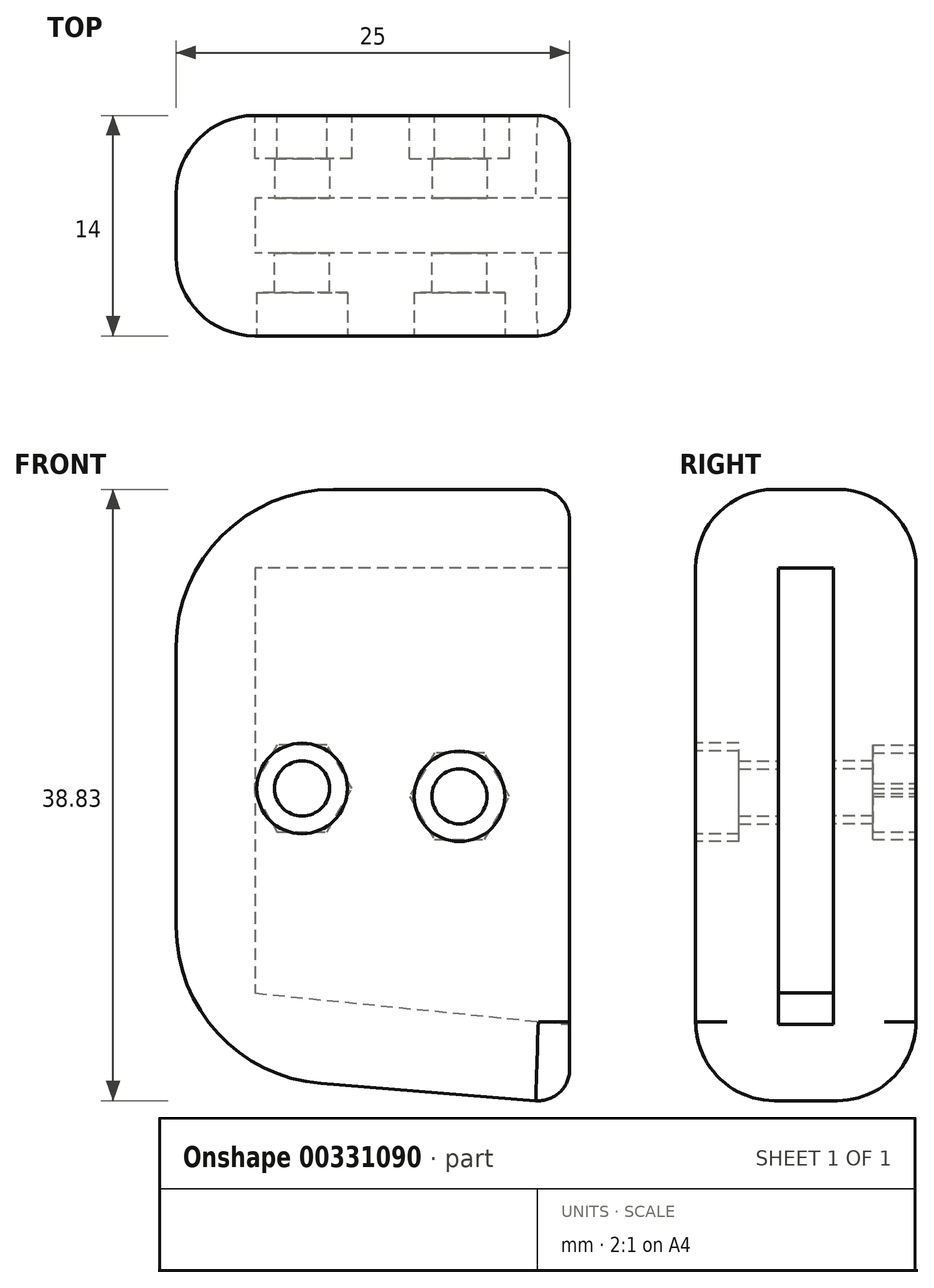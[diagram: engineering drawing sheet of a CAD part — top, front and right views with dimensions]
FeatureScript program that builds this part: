
annotation { "Feature Type Name" : "Feature", "Feature Type Description" : "" }
export const myFeature = defineFeature(function(context is Context, id is Id, definition is map)
    precondition{}
    {
        {
            var Q0;
            Q0=qCreatedBy(makeId("Front.planeOp"),FACE);
            var sketch = newSketch(context, id + "F0", { "sketchPlane" : qUnion([Q0])});
            skLineSegment(sketch, "E0", {"start": v(0, 0) * mm, "end": v(25, 0) * mm});
            skLineSegment(sketch, "E1", {"start": v(25, 0) * mm, "end": v(25, -39) * mm});
            skLineSegment(sketch, "E2", {"start": v(25, -39) * mm, "end": v(0, -37) * mm});
            skLineSegment(sketch, "E3", {"start": v(0, -37) * mm, "end": v(0, 0) * mm});
            skSolve(sketch);
        }
        {
            var Q0;
            Q0=makeQuery(id+"F0.imprint","IMPRINT",FACE,{"disambiguationData":[TD([[makeQuery(id+"F0.imprint","IMPRINT",EDGE,{"derivedFrom":sQuery(id+"F0.wireOp",EDGE,"E0")}),-1.0]])]});
            extrude(context, id + "F1", {"entities" : qUnion([Q0]), "depth" : 7 * mm});
        }
        {
            var Q0;
            Q0=makeQuery(id+"F1.opExtrude","CAP_FACE",FACE,{"disambiguationData":[OSD([sQuery(id+"F0.wireOp",EDGE,"E0"),sQuery(id+"F0.wireOp",EDGE,"E1"),sQuery(id+"F0.wireOp",EDGE,"E2"),sQuery(id+"F0.wireOp",EDGE,"E3")])],"isStart":false});
            var sketch = newSketch(context, id + "F2", { "sketchPlane" : qUnion([Q0])});
            skLineSegment(sketch, "E4", {"start": v(25, -5) * mm, "end": v(5, -5) * mm});
            skLineSegment(sketch, "E5", {"start": v(5, -5) * mm, "end": v(5, -32) * mm});
            skLineSegment(sketch, "E6", {"start": v(5, -32) * mm, "end": v(25, -34) * mm});
            skSolve(sketch);
        }
        {
            var Q0;
            {var subQ0=sQuery(id+"F2.wireOp",EDGE,"E4");Q0=makeQuery(id+"F2.imprint","IMPRINT",FACE,{"disambiguationData":[TD([[makeQuery(id+"F2.imprint","IMPRINT",EDGE,{"derivedFrom":subQ0}),1.0]])]});}
            extrude(context, id + "F3", {"entities" : qUnion([Q0]), "operationType" : NewBodyOperationType.REMOVE, "oppositeDirection" : true, "depth" : 1.75 * mm});
        }
        {
            var Q0;
            Q0=makeQuery(id+"F3.boolean.opBoolean","COPY",FACE,{"derivedFrom":makeQuery(id+"F3.opExtrude","CAP_FACE",FACE,{"disambiguationData":[OSD([sQuery(id+"F0.wireOp",EDGE,"E1"),sQuery(id+"F2.wireOp",EDGE,"E4"),sQuery(id+"F2.wireOp",EDGE,"E5"),sQuery(id+"F2.wireOp",EDGE,"E6")])],"isStart":false})});
            var sketch = newSketch(context, id + "F4", { "sketchPlane" : qUnion([Q0])});
            skLineSegment(sketch, "E7", {"start": v(25, -19.5) * mm, "end": v(5, -19.5) * mm, "construction": true});
            skCircle(sketch, "E8", {"center": v(18, -19.5) * mm, "radius": 1.75 * mm});
            skLineSegment(sketch, "E9", {"start": v(25, -19) * mm, "end": v(5, -19) * mm, "construction": true});
            skCircle(sketch, "E10", {"center": v(8, -19) * mm, "radius": 1.75 * mm});
            skSolve(sketch);
        }
        {
            var Q0;
            Q0=makeQuery(id+"F4.imprint","IMPRINT",FACE,{"disambiguationData":[TD([[makeQuery(id+"F4.imprint","IMPRINT",EDGE,{"derivedFrom":sQuery(id+"F4.wireOp",EDGE,"E10")}),1.0]])]});
            var Q1;
            Q1=makeQuery(id+"F4.imprint","IMPRINT",FACE,{"disambiguationData":[TD([[makeQuery(id+"F4.imprint","IMPRINT",EDGE,{"derivedFrom":sQuery(id+"F4.wireOp",EDGE,"E8")}),1.0]])]});
            extrude(context, id + "F5", {"entities" : qUnion([Q0, Q1]), "operationType" : NewBodyOperationType.REMOVE, "oppositeDirection" : true, "depth" : 5.25 * mm});
        }
        {
            var Q0;
            Q0=makeQuery(id+"F1.opExtrude","SWEPT_BODY",BODY,{"disambiguationData":[OSD([sQuery(id+"F0.wireOp",EDGE,"E0"),sQuery(id+"F0.wireOp",EDGE,"E1"),sQuery(id+"F0.wireOp",EDGE,"E2"),sQuery(id+"F0.wireOp",EDGE,"E3")])]});
            var Q1;
            Q1=makeQuery(id+"F1.opExtrude","CAP_FACE",FACE,{"disambiguationData":[OSD([sQuery(id+"F0.wireOp",EDGE,"E0"),sQuery(id+"F0.wireOp",EDGE,"E1"),sQuery(id+"F0.wireOp",EDGE,"E2"),sQuery(id+"F0.wireOp",EDGE,"E3")])],"isStart":false});
            mirror(context, id + "F6", {"operationType" : NewBodyOperationType.ADD, "entities" : qUnion([Q0]), "mirrorPlane" : qUnion([Q1])});
        }
        {
            var Q0;
            {var subQ0=makeQuery(id+"F1.opExtrude","SWEPT_EDGE",EDGE,{"disambiguationData":[OSD([sQuery(id+"F0.wireOp",EDGE,"E0"),sQuery(id+"F0.wireOp",EDGE,"E3")])]});Q0=makeQuery(id+"F6.boolean.opBoolean","MERGE",EDGE,{"derivedFrom":[subQ0,makeQuery(id+"F6.opPattern","COPY",EDGE,{"derivedFrom":subQ0,"instanceName":"1"})]});}
            var Q1;
            {var subQ0=makeQuery(id+"F1.opExtrude","SWEPT_EDGE",EDGE,{"disambiguationData":[OSD([sQuery(id+"F0.wireOp",EDGE,"E2"),sQuery(id+"F0.wireOp",EDGE,"E3")])]});Q1=makeQuery(id+"F6.boolean.opBoolean","MERGE",EDGE,{"derivedFrom":[subQ0,makeQuery(id+"F6.opPattern","COPY",EDGE,{"derivedFrom":subQ0,"instanceName":"1"})]});}
            fillet(context, id + "F7", {"entities" : qUnion([Q0, Q1]), "radius" : 10 * mm, "tangentPropagation" : true, "allowEdgeOverflow" : false});
        }
        {
            var Q0;
            Q0=makeQuery(id+"F6.opPattern","COPY",EDGE,{"derivedFrom":makeQuery(id+"F1.opExtrude","CAP_EDGE",EDGE,{"disambiguationData":[OSD([sQuery(id+"F0.wireOp",EDGE,"E0")])],"isStart":true}),"instanceName":"1"});
            var Q1;
            Q1=makeQuery(id+"F1.opExtrude","CAP_EDGE",EDGE,{"disambiguationData":[OSD([sQuery(id+"F0.wireOp",EDGE,"E0")])],"isStart":true});
            fillet(context, id + "F8", {"entities" : qUnion([Q0, Q1]), "radius" : 5 * mm, "tangentPropagation" : true, "allowEdgeOverflow" : false});
        }
        {
            var Q0;
            Q0=makeQuery(id+"F6.opPattern","COPY",EDGE,{"derivedFrom":makeQuery(id+"F1.opExtrude","CAP_EDGE",EDGE,{"disambiguationData":[OSD([sQuery(id+"F0.wireOp",EDGE,"E1")])],"isStart":true}),"instanceName":"1"});
            fillet(context, id + "F9", {"entities" : qUnion([Q0]), "radius" : 2 * mm, "tangentPropagation" : true, "allowEdgeOverflow" : false});
        }
        {
            var Q0;
            Q0=makeQuery(id+"F6.opPattern","COPY",FACE,{"derivedFrom":makeQuery(id+"F1.opExtrude","CAP_FACE",FACE,{"disambiguationData":[OSD([sQuery(id+"F0.wireOp",EDGE,"E0"),sQuery(id+"F0.wireOp",EDGE,"E1"),sQuery(id+"F0.wireOp",EDGE,"E2"),sQuery(id+"F0.wireOp",EDGE,"E3")])],"isStart":true}),"instanceName":"1"});
            var sketch = newSketch(context, id + "F10", { "sketchPlane" : qUnion([Q0])});
            skCircle(sketch, "E11", {"center": v(8, -19) * mm, "radius": 2.88 * mm});
            skCircle(sketch, "E12", {"center": v(18, -19.5) * mm, "radius": 2.88 * mm});
            skSolve(sketch);
        }
        {
            var Q0;
            Q0=makeQuery(id+"F10.imprint","IMPRINT",FACE,{"disambiguationData":[TD([[makeQuery(id+"F10.imprint","IMPRINT",EDGE,{"derivedFrom":sQuery(id+"F10.wireOp",EDGE,"E11")}),1.0]])]});
            var Q1;
            Q1=makeQuery(id+"F10.imprint","IMPRINT",FACE,{"disambiguationData":[TD([[makeQuery(id+"F10.imprint","IMPRINT",EDGE,{"derivedFrom":sQuery(id+"F10.wireOp",EDGE,"E12")}),1.0]])]});
            extrude(context, id + "F11", {"entities" : qUnion([Q0, Q1]), "operationType" : NewBodyOperationType.REMOVE, "oppositeDirection" : true, "depth" : 2.75 * mm});
        }
        {
            var Q0;
            Q0=makeQuery(id+"F1.opExtrude","CAP_FACE",FACE,{"disambiguationData":[OSD([sQuery(id+"F0.wireOp",EDGE,"E0"),sQuery(id+"F0.wireOp",EDGE,"E1"),sQuery(id+"F0.wireOp",EDGE,"E2"),sQuery(id+"F0.wireOp",EDGE,"E3")])],"isStart":true});
            var sketch = newSketch(context, id + "F12", { "sketchPlane" : qUnion([Q0])});
            skCircle(sketch, "E13.cCircle", {"center": v(-18, -19.5) * mm, "radius": 2.75 * mm, "construction": true});
            skLineSegment(sketch, "E13.0", {"start": v(-19.59, -16.75) * mm, "end": v(-16.41, -16.75) * mm});
            skLineSegment(sketch, "E13.1", {"start": v(-16.41, -16.75) * mm, "end": v(-14.82, -19.5) * mm});
            skLineSegment(sketch, "E13.2", {"start": v(-14.82, -19.5) * mm, "end": v(-16.41, -22.25) * mm});
            skLineSegment(sketch, "E13.3", {"start": v(-16.41, -22.25) * mm, "end": v(-19.59, -22.25) * mm});
            skLineSegment(sketch, "E13.4", {"start": v(-19.59, -22.25) * mm, "end": v(-21.18, -19.5) * mm});
            skLineSegment(sketch, "E13.5", {"start": v(-21.18, -19.5) * mm, "end": v(-19.59, -16.75) * mm});
            skPoint(sketch, "E13.0.midPoint", {"position": v(-18, -16.75) * mm});
            skCircle(sketch, "E14.cCircle", {"center": v(-8, -19) * mm, "radius": 2.75 * mm, "construction": true});
            skLineSegment(sketch, "E14.0", {"start": v(-9.59, -16.25) * mm, "end": v(-6.41, -16.25) * mm});
            skLineSegment(sketch, "E14.1", {"start": v(-6.41, -16.25) * mm, "end": v(-4.82, -19) * mm});
            skLineSegment(sketch, "E14.2", {"start": v(-4.82, -19) * mm, "end": v(-6.41, -21.75) * mm});
            skLineSegment(sketch, "E14.3", {"start": v(-6.41, -21.75) * mm, "end": v(-9.59, -21.75) * mm});
            skLineSegment(sketch, "E14.4", {"start": v(-9.59, -21.75) * mm, "end": v(-11.18, -19) * mm});
            skLineSegment(sketch, "E14.5", {"start": v(-11.18, -19) * mm, "end": v(-9.59, -16.25) * mm});
            skPoint(sketch, "E14.0.midPoint", {"position": v(-8, -16.25) * mm});
            skSolve(sketch);
        }
        {
            var Q0;
            Q0=makeQuery(id+"F12.imprint","IMPRINT",FACE,{"disambiguationData":[TD([[makeQuery(id+"F12.imprint","IMPRINT",EDGE,{"derivedFrom":sQuery(id+"F12.wireOp",EDGE,"E13.0")}),-1.0]])]});
            var Q1;
            {var subQ6=sQuery(id+"F12.wireOp",EDGE,"E14.0");Q1=makeQuery(id+"F12.imprint","IMPRINT",FACE,{"disambiguationData":[TD([[makeQuery(id+"F12.imprint","IMPRINT",EDGE,{"derivedFrom":subQ6}),-1.0]])]});}
            extrude(context, id + "F13", {"entities" : qUnion([Q0, Q1]), "operationType" : NewBodyOperationType.REMOVE, "oppositeDirection" : true, "depth" : 2.75 * mm});
        }
    });
